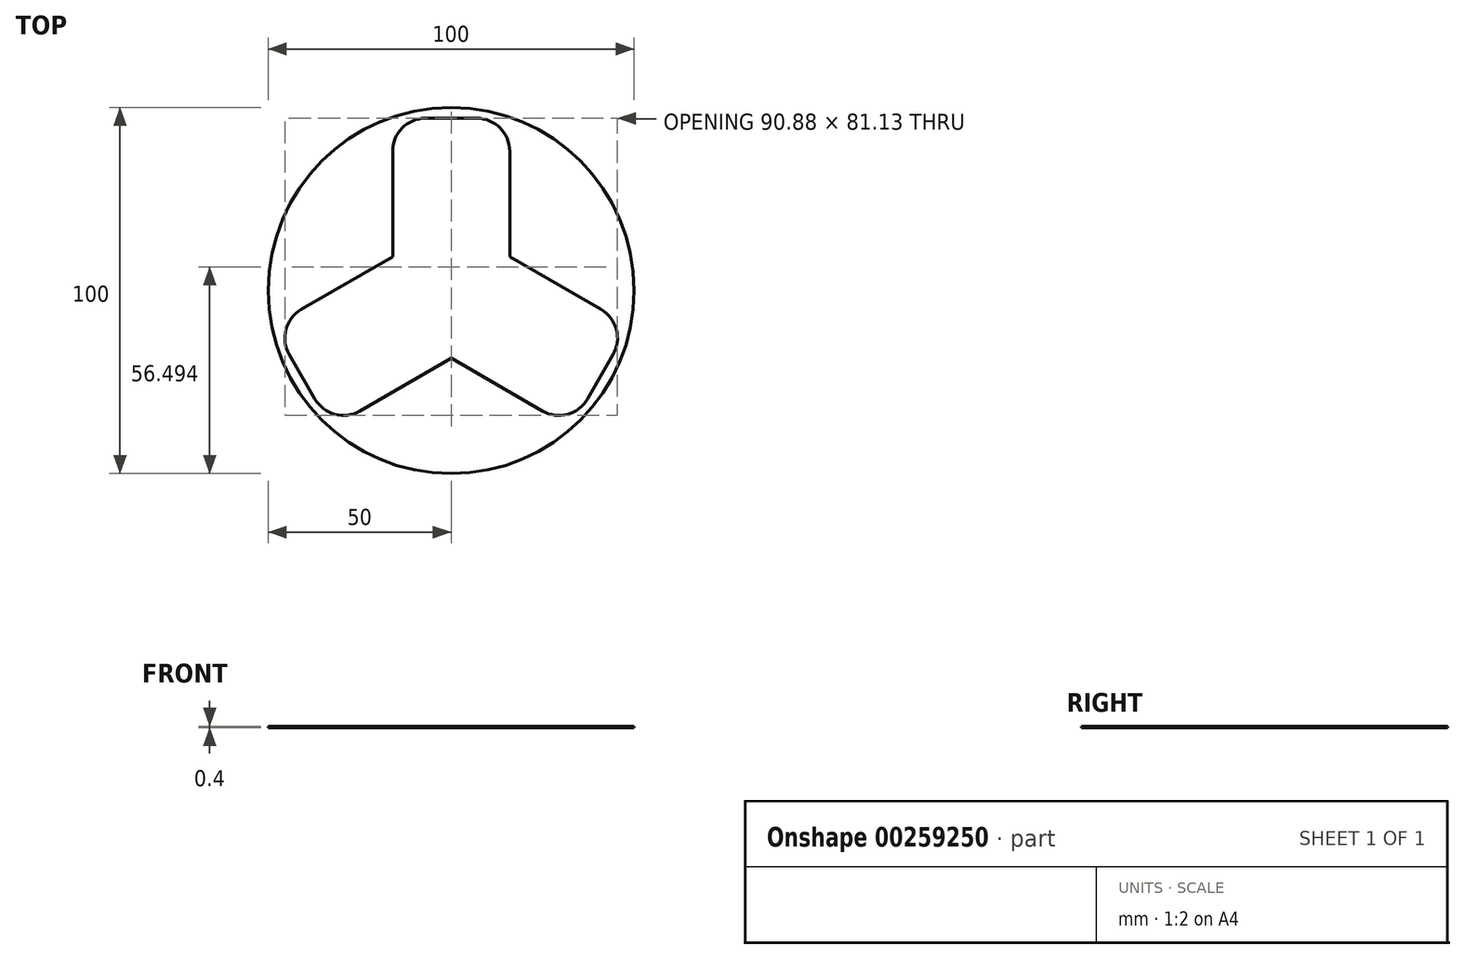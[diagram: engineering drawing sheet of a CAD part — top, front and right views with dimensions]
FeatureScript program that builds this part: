
annotation { "Feature Type Name" : "Feature", "Feature Type Description" : "" }
export const myFeature = defineFeature(function(context is Context, id is Id, definition is map)
    precondition{}
    {
        {
            var Q0;
            Q0=qCreatedBy(makeId("Top.planeOp"),FACE);
            var sketch = newSketch(context, id + "F0", { "sketchPlane" : qUnion([Q0])});
            skLineSegment(sketch, "E0.bottom", {"start": v(-7, 47.06) * mm, "end": v(7, 47.06) * mm});
            skLineSegment(sketch, "E0.top", {"start": v(-13, 5.06) * mm, "end": v(13, 5.06) * mm});
            skLineSegment(sketch, "E0.left", {"start": v(-16, 38.06) * mm, "end": v(-16, 8.06) * mm});
            skLineSegment(sketch, "E0.right", {"start": v(16, 38.06) * mm, "end": v(16, 8.06) * mm});
            skPoint(sketch, "E1.visualSharp", {"position": v(-16, 5.06) * mm});
            skArc(sketch, "E1.filletArc", {"start": v(-16, 8.06) * mm, "mid": v(-15.12, 5.94) * mm, "end": v(-13, 5.06) * mm});
            skPoint(sketch, "E2.visualSharp", {"position": v(16, 5.06) * mm});
            skArc(sketch, "E2.filletArc", {"start": v(13, 5.06) * mm, "mid": v(15.12, 5.94) * mm, "end": v(16, 8.06) * mm});
            skPoint(sketch, "E3.visualSharp", {"position": v(-16, 47.06) * mm});
            skArc(sketch, "E3.filletArc", {"start": v(-7, 47.06) * mm, "mid": v(-13.36, 44.42) * mm, "end": v(-16, 38.06) * mm});
            skPoint(sketch, "E4.visualSharp", {"position": v(16, 47.06) * mm});
            skArc(sketch, "E4.filletArc", {"start": v(16, 38.06) * mm, "mid": v(13.36, 44.42) * mm, "end": v(7, 47.06) * mm});
            skPoint(sketch, "E5", {"position": v(0, 47.06) * mm});
            skSolve(sketch);
        }
        {
            var Q0;
            Q0=qCreatedBy(makeId("Top.planeOp"),FACE);
            var sketch = newSketch(context, id + "F1", { "sketchPlane" : qUnion([Q0])});
            skCircle(sketch, "E6", {"center": v(0, 0) * mm, "radius": 50 * mm});
            skArc(sketch, "E7.0.0", {"start": v(-16, 8.06) * mm, "mid": v(-15.12, 5.94) * mm, "end": v(-13, 5.06) * mm});
            skLineSegment(sketch, "E7.0.1", {"start": v(-13, 5.06) * mm, "end": v(13, 5.06) * mm});
            skArc(sketch, "E7.0.2", {"start": v(13, 5.06) * mm, "mid": v(15.12, 5.94) * mm, "end": v(16, 8.06) * mm});
            skLineSegment(sketch, "E7.0.3", {"start": v(16, 8.06) * mm, "end": v(16, 38.06) * mm});
            skArc(sketch, "E7.0.4", {"start": v(16, 38.06) * mm, "mid": v(13.36, 44.42) * mm, "end": v(7, 47.06) * mm});
            skLineSegment(sketch, "E7.0.5", {"start": v(7, 47.06) * mm, "end": v(-7, 47.06) * mm});
            skArc(sketch, "E7.0.6", {"start": v(-7, 47.06) * mm, "mid": v(-13.36, 44.42) * mm, "end": v(-16, 38.06) * mm});
            skLineSegment(sketch, "E7.0.7", {"start": v(-16, 38.06) * mm, "end": v(-16, 8.06) * mm});
            skLineSegment(sketch, "E8.1.0", {"start": v(2.12, -13.79) * mm, "end": v(-10.88, 8.73) * mm});
            skLineSegment(sketch, "E8.1.1", {"start": v(-14.98, 9.83) * mm, "end": v(-40.96, -5.17) * mm});
            skArc(sketch, "E8.1.2", {"start": v(-40.96, -5.17) * mm, "mid": v(-45.15, -10.64) * mm, "end": v(-44.26, -17.47) * mm});
            skLineSegment(sketch, "E8.1.3", {"start": v(-44.26, -17.47) * mm, "end": v(-37.26, -29.6) * mm});
            skArc(sketch, "E8.1.4", {"start": v(-37.26, -29.6) * mm, "mid": v(-31.8, -33.79) * mm, "end": v(-24.96, -32.89) * mm});
            skLineSegment(sketch, "E8.1.5", {"start": v(-24.96, -32.89) * mm, "end": v(1.02, -17.89) * mm});
            skArc(sketch, "E8.1.6", {"start": v(1.02, -17.89) * mm, "mid": v(2.42, -16.06) * mm, "end": v(2.12, -13.79) * mm});
            skArc(sketch, "E8.1.7", {"start": v(-10.88, 8.73) * mm, "mid": v(-12.7, 10.13) * mm, "end": v(-14.98, 9.83) * mm});
            skLineSegment(sketch, "E8.2.0", {"start": v(10.88, 8.73) * mm, "end": v(-2.12, -13.79) * mm});
            skLineSegment(sketch, "E8.2.1", {"start": v(-1.02, -17.89) * mm, "end": v(24.96, -32.89) * mm});
            skArc(sketch, "E8.2.2", {"start": v(24.96, -32.89) * mm, "mid": v(31.8, -33.79) * mm, "end": v(37.26, -29.6) * mm});
            skLineSegment(sketch, "E8.2.3", {"start": v(37.26, -29.6) * mm, "end": v(44.26, -17.47) * mm});
            skArc(sketch, "E8.2.4", {"start": v(44.26, -17.47) * mm, "mid": v(45.15, -10.64) * mm, "end": v(40.96, -5.17) * mm});
            skLineSegment(sketch, "E8.2.5", {"start": v(40.96, -5.17) * mm, "end": v(14.98, 9.83) * mm});
            skArc(sketch, "E8.2.6", {"start": v(14.98, 9.83) * mm, "mid": v(12.7, 10.13) * mm, "end": v(10.88, 8.73) * mm});
            skArc(sketch, "E8.2.7", {"start": v(-2.12, -13.79) * mm, "mid": v(-2.42, -16.06) * mm, "end": v(-1.02, -17.89) * mm});
            skSolve(sketch);
        }
        {
            var Q0;
            Q0=makeQuery(id+"F1.imprint","IMPRINT",FACE,{"disambiguationData":[TD([[makeQuery(id+"F1.imprint","IMPRINT",EDGE,{"derivedFrom":sQuery(id+"F1.wireOp",EDGE,"E6")}),1.0]])]});
            extrude(context, id + "F2", {"entities" : qUnion([Q0]), "depth" : 0.4 * mm, "offsetDistance" : 25.4 * mm});
        }
    });
